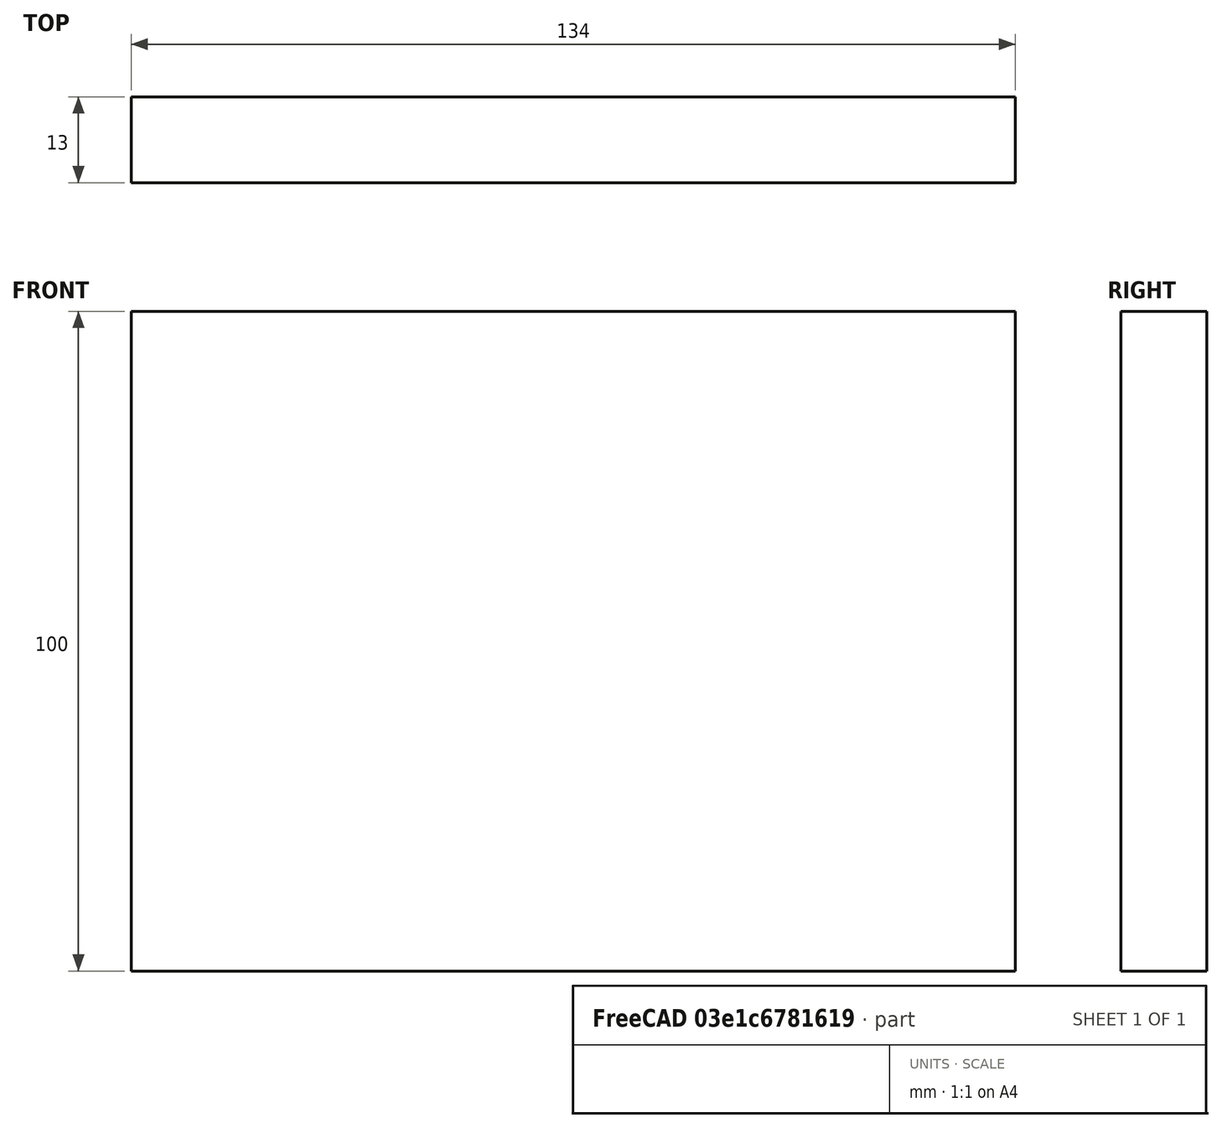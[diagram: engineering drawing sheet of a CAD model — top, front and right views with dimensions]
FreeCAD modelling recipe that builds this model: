
FCSTD DOCUMENT  (FreeCAD 0.18R14555 (Git shallow))
Label: 1001_keyboard_sidewall_16_
License: All rights reserved
LicenseURL: http://en.wikipedia.org/wiki/All_rights_reserved
objects: Sketcher::SketchObject×1, PartDesign::Pad×1, PartDesign::Body×1, Spreadsheet::Sheet×1
note: 4 computed .brp shape members not serialized (recipe doc carries the construction recipe); baked Part::Feature solids carry a one-line shape summary decoded from their .brp

FEATURE [Sketcher::SketchObject] Sketch  label="SideWall"
  MapMode = 5
  Placement = pos=(0,0,0) rot=(1,0,0;1.5708rad)
  Support = -> [XZ_Plane]
  expr: Constraints[10] = xls.X0
  expr: Constraints.z_0 = xls.z_0
  sketch-geometry (4):
    g0: LineSegment StartX=134 StartY=0 StartZ=0 EndX=0 EndY=0 EndZ=0
    g1: LineSegment StartX=0 StartY=0 StartZ=0 EndX=0 EndY=100 EndZ=0
    g2: LineSegment StartX=0 StartY=100 StartZ=0 EndX=134 EndY=100 EndZ=0
    g3: LineSegment StartX=134 StartY=100 StartZ=0 EndX=134 EndY=0 EndZ=0
  constraints (11):
    c: Coincident(g0,g-1)
    c: Horizontal(g0)
    c: Coincident(g1,g-1)
    c: Vertical(g1)
    c: Coincident(g2,g1)
    c: Vertical(g3)
    c: Coincident(g0,g3)
    c: Perpendicular(g1,g2)
    c: DistanceY(g1,g1) = 100  'z_0'
    c: Coincident(g3,g2)
    c: DistanceX(g2,g2) = 134
FEATURE [PartDesign::Pad] Pad
  Length = 13
  Length2 = 13
  Placement = pos=(0,0,0) rot=(1,0,0;1.5708rad)
  Profile = -> Sketch
  Reversed = true
  Type = 0
FEATURE [PartDesign::Body] Body
  Group = -> [Sketch,Pad]
  Origin = -> Origin
  Tip = -> Pad
FEATURE [Spreadsheet::Sheet] Spreadsheet  label="xls"
  cells = C2=INHERITED DIMENSIONS; C3=Thickness; D3=kbf_t_0; E3=16; F3=mm; H3=NOTE: No plexi; C5=SIDEWALL ; C6=thickness of board; D6=t; E6(nt)=16; F6=mm; C7=Depth of Board; E7=150; G7=NOMINAL; C8=Depth of board; D8=X0; E8(X0)==+E7 - E3; F8=mm; G8=REAL; C9=Height of board; D9=Z0; E9(z_0)=100; F9=mm
